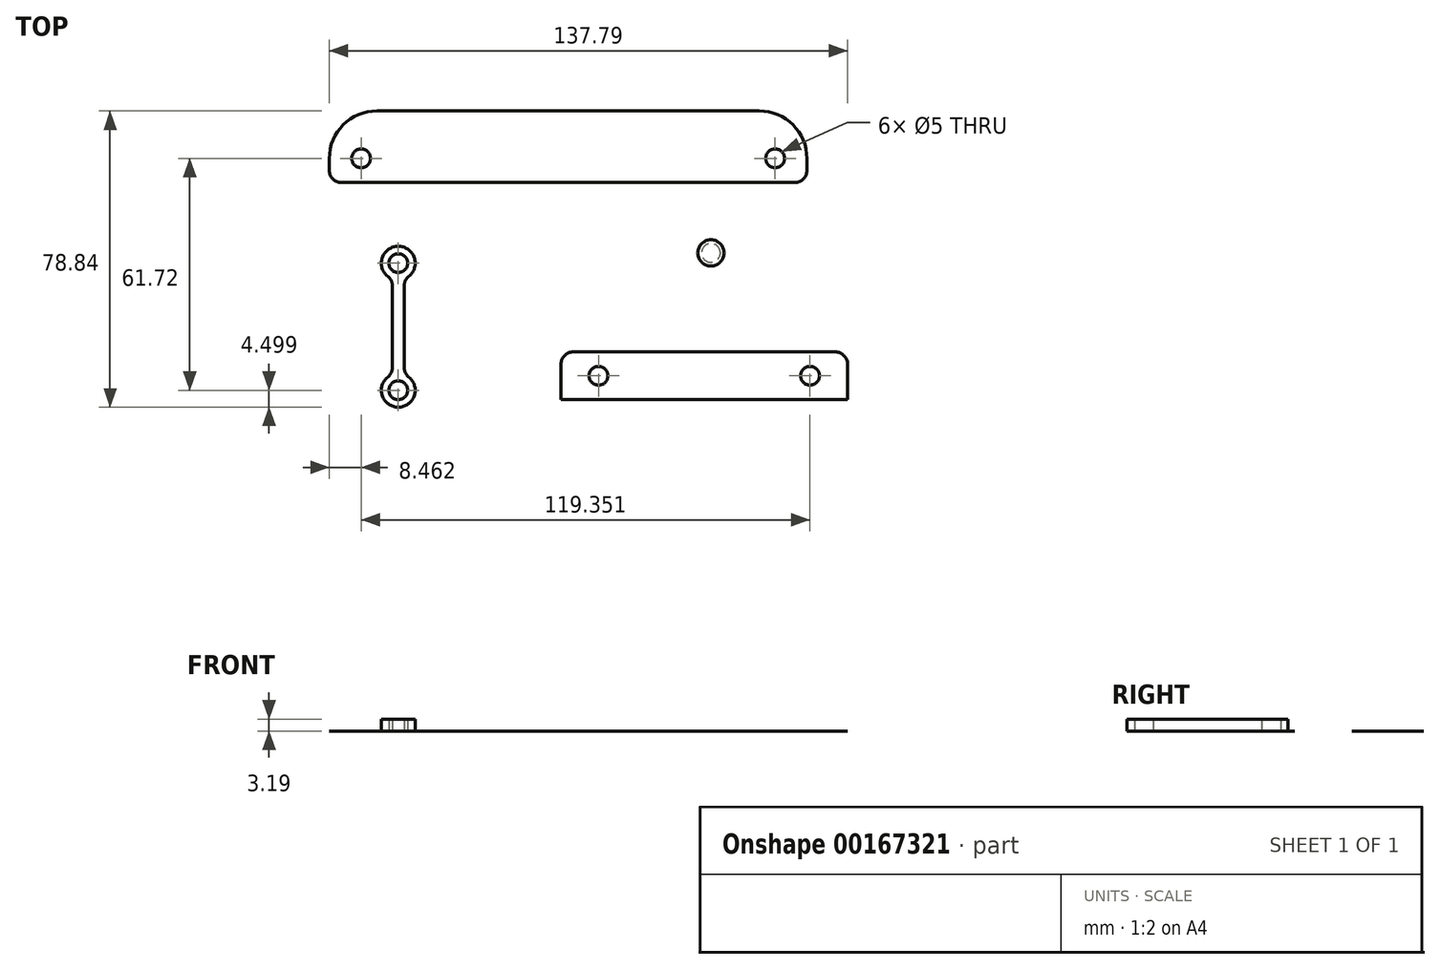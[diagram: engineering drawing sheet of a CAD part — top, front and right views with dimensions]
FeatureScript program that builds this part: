
annotation { "Feature Type Name" : "Feature", "Feature Type Description" : "" }
export const myFeature = defineFeature(function(context is Context, id is Id, definition is map)
    precondition{}
    {
        {
            var Q0;
            Q0=qCreatedBy(makeId("Top.planeOp"),FACE);
            var sketch = newSketch(context, id + "F0", { "sketchPlane" : qUnion([Q0])});
            skCircle(sketch, "E0", {"center": v(-35.3, 16.91) * mm, "radius": 2.5 * mm});
            skArc(sketch, "E1", {"start": v(-32.5, 13.38) * mm, "mid": v(-35.3, 21.41) * mm, "end": v(-38.09, 13.38) * mm});
            skLineSegment(sketch, "E2.bottom", {"start": v(-33.71, 0) * mm, "end": v(-36.88, 0) * mm});
            skLineSegment(sketch, "E2.left", {"start": v(-33.71, 0) * mm, "end": v(-33.71, 10.9) * mm});
            skLineSegment(sketch, "E2.right", {"start": v(-36.88, 0) * mm, "end": v(-36.88, 10.9) * mm});
            skPoint(sketch, "E3.visualSharp", {"position": v(-36.88, 12.7) * mm});
            skArc(sketch, "E3.filletArc", {"start": v(-36.88, 10.9) * mm, "mid": v(-37.2, 12.27) * mm, "end": v(-38.09, 13.38) * mm});
            skPoint(sketch, "E4.visualSharp", {"position": v(-33.71, 12.7) * mm});
            skArc(sketch, "E4.filletArc", {"start": v(-32.5, 13.38) * mm, "mid": v(-33.4, 12.27) * mm, "end": v(-33.71, 10.9) * mm});
            skArc(sketch, "E5.MirrorCS", {"start": v(-36.88, -10.9) * mm, "mid": v(-37.2, -12.27) * mm, "end": v(-38.09, -13.38) * mm});
            skPoint(sketch, "E6.MirrorP", {"position": v(-36.88, -12.7) * mm});
            skCircle(sketch, "E7.MirrorC", {"center": v(-35.3, -16.91) * mm, "radius": 2.5 * mm});
            skLineSegment(sketch, "E8.MirrorCS", {"start": v(-33.71, 0) * mm, "end": v(-33.71, -10.9) * mm});
            skLineSegment(sketch, "E9.MirrorCS", {"start": v(-36.88, 0) * mm, "end": v(-36.88, -10.9) * mm});
            skArc(sketch, "E10.MirrorCS", {"start": v(-32.5, -13.38) * mm, "mid": v(-33.4, -12.27) * mm, "end": v(-33.71, -10.9) * mm});
            skArc(sketch, "E11.MirrorCS", {"start": v(-32.5, -13.38) * mm, "mid": v(-35.3, -21.41) * mm, "end": v(-38.09, -13.38) * mm});
            skPoint(sketch, "E12.MirrorP", {"position": v(-33.71, -12.7) * mm});
            skSolve(sketch);
        }
        {
            var Q0;
            Q0 = qSketchRegion(id + "F0", true);
            extrude(context, id + "F1", {"entities" : qUnion([Q0]), "depth" : 3.17 * mm});
        }
        {
            var Q0;
            Q0=qCreatedBy(makeId("Top.planeOp"),FACE);
            var sketch = newSketch(context, id + "F2", { "sketchPlane" : qUnion([Q0])});
            skLineSegment(sketch, "E13.bottom", {"start": v(-50.47, 38.38) * mm, "end": v(9.86, 38.38) * mm});
            skLineSegment(sketch, "E13.top", {"start": v(-40.94, 57.43) * mm, "end": v(9.86, 57.43) * mm});
            skLineSegment(sketch, "E13.left", {"start": v(-53.64, 41.56) * mm, "end": v(-53.64, 44.73) * mm});
            skLineSegment(sketch, "E13.right", {"start": v(9.86, 38.38) * mm, "end": v(9.86, 57.43) * mm, "construction": true});
            skCircle(sketch, "E14", {"center": v(-45.18, 44.8) * mm, "radius": 2.5 * mm});
            skPoint(sketch, "E15.visualSharp", {"position": v(-53.64, 57.43) * mm});
            skArc(sketch, "E15.filletArc", {"start": v(-40.94, 57.43) * mm, "mid": v(-49.92, 53.71) * mm, "end": v(-53.64, 44.73) * mm});
            skPoint(sketch, "E16.visualSharp", {"position": v(-53.64, 38.38) * mm});
            skArc(sketch, "E16.filletArc", {"start": v(-53.64, 41.56) * mm, "mid": v(-52.71, 39.31) * mm, "end": v(-50.47, 38.38) * mm});
            skLineSegment(sketch, "E17.MirrorCS", {"start": v(70.18, 38.38) * mm, "end": v(9.86, 38.38) * mm});
            skLineSegment(sketch, "E18.MirrorCS", {"start": v(60.66, 57.43) * mm, "end": v(9.86, 57.43) * mm});
            skLineSegment(sketch, "E19.MirrorCS", {"start": v(73.36, 41.56) * mm, "end": v(73.36, 44.73) * mm});
            skArc(sketch, "E20.MirrorCS", {"start": v(73.36, 41.56) * mm, "mid": v(72.43, 39.31) * mm, "end": v(70.18, 38.38) * mm});
            skCircle(sketch, "E21.MirrorC", {"center": v(64.9, 44.8) * mm, "radius": 2.5 * mm});
            skPoint(sketch, "E22.MirrorP", {"position": v(73.36, 38.38) * mm});
            skArc(sketch, "E23.MirrorCS", {"start": v(60.66, 57.43) * mm, "mid": v(69.64, 53.71) * mm, "end": v(73.36, 44.73) * mm});
            skPoint(sketch, "E24.MirrorP", {"position": v(73.36, 57.43) * mm});
            skSolve(sketch);
        }
        {
            var Q0;
            Q0 = qSketchRegion(id + "F2", true);
            extrude(context, id + "F3", {"entities" : qUnion([Q0]), "depth" : 1 / 203.2 * mm});
        }
        {
            var Q0;
            Q0=qCreatedBy(makeId("Top.planeOp"),FACE);
            var sketch = newSketch(context, id + "F4", { "sketchPlane" : qUnion([Q0])});
            skCircle(sketch, "E25", {"center": v(47.83, 19.63) * mm, "radius": 2.5 * mm});
            skCircle(sketch, "E26", {"center": v(47.83, 19.63) * mm, "radius": 3.5 * mm});
            skSolve(sketch);
        }
        {
            var Q0;
            Q0=makeQuery(id+"F4.imprint","IMPRINT",FACE,{"disambiguationData":[TD([[makeQuery(id+"F4.imprint","IMPRINT",EDGE,{"derivedFrom":sQuery(id+"F4.wireOp",EDGE,"E25")}),1.0]])]});
            extrude(context, id + "F5", {"entities" : qUnion([Q0]), "oppositeDirection" : true, "depth" : 1 / 101.6 * mm});
        }
        {
            var Q0;
            Q0=makeQuery(id+"F4.imprint","IMPRINT",FACE,{"disambiguationData":[TD([[makeQuery(id+"F4.imprint","IMPRINT",EDGE,{"derivedFrom":sQuery(id+"F4.wireOp",EDGE,"E25")}),1.0]])]});
            var Q1;
            Q1=makeQuery(id+"F4.imprint","IMPRINT",FACE,{"disambiguationData":[TD([[makeQuery(id+"F4.imprint","IMPRINT",EDGE,{"derivedFrom":sQuery(id+"F4.wireOp",EDGE,"E25")}),-1.0]])]});
            extrude(context, id + "F6", {"entities" : qUnion([Q0, Q1]), "operationType" : NewBodyOperationType.ADD, "depth" : 1 / 203.2 * mm});
        }
        {
            var Q0;
            Q0=qCreatedBy(makeId("Top.planeOp"),FACE);
            var sketch = newSketch(context, id + "F7", { "sketchPlane" : qUnion([Q0])});
            skLineSegment(sketch, "E27.bottom", {"start": v(11.24, -6.7) * mm, "end": v(46.05, -6.7) * mm});
            skLineSegment(sketch, "E27.top", {"start": v(7.95, -19.4) * mm, "end": v(46.05, -19.4) * mm});
            skLineSegment(sketch, "E27.left", {"start": v(7.95, -10) * mm, "end": v(7.95, -19.4) * mm});
            skLineSegment(sketch, "E27.right", {"start": v(46.05, -6.7) * mm, "end": v(46.05, -19.4) * mm, "construction": true});
            skPoint(sketch, "E28.visualSharp", {"position": v(7.95, -6.7) * mm});
            skArc(sketch, "E28.filletArc", {"start": v(11.24, -6.7) * mm, "mid": v(8.92, -7.67) * mm, "end": v(7.95, -10) * mm});
            skCircle(sketch, "E29", {"center": v(17.94, -13.06) * mm, "radius": 2.5 * mm});
            skLineSegment(sketch, "E30", {"start": v(17.94, -13.06) * mm, "end": v(17.94, -19.4) * mm});
            skLineSegment(sketch, "E31", {"start": v(17.94, -19.4) * mm, "end": v(17.94, -13.06) * mm, "construction": true});
            skLineSegment(sketch, "E32", {"start": v(17.94, -13.06) * mm, "end": v(17.94, -6.7) * mm, "construction": true});
            skLineSegment(sketch, "E33.MirrorCS", {"start": v(74.17, -13.06) * mm, "end": v(74.17, -19.4) * mm});
            skLineSegment(sketch, "E34.MirrorCS", {"start": v(80.86, -6.7) * mm, "end": v(46.05, -6.7) * mm});
            skLineSegment(sketch, "E35.MirrorCS", {"start": v(84.15, -19.4) * mm, "end": v(46.05, -19.4) * mm});
            skLineSegment(sketch, "E36.MirrorCS", {"start": v(84.15, -10) * mm, "end": v(84.15, -19.4) * mm});
            skLineSegment(sketch, "E37.MirrorCS", {"start": v(74.17, -13.06) * mm, "end": v(74.17, -6.7) * mm, "construction": true});
            skLineSegment(sketch, "E38.MirrorCS", {"start": v(74.17, -19.4) * mm, "end": v(74.17, -13.06) * mm, "construction": true});
            skPoint(sketch, "E39.MirrorP", {"position": v(84.15, -6.7) * mm});
            skCircle(sketch, "E40.MirrorC", {"center": v(74.17, -13.06) * mm, "radius": 2.5 * mm});
            skArc(sketch, "E41.MirrorCS", {"start": v(80.86, -6.7) * mm, "mid": v(83.2, -7.67) * mm, "end": v(84.15, -10) * mm});
            skSolve(sketch);
        }
        {
            var Q0;
            Q0 = qSketchRegion(id + "F7", true);
            extrude(context, id + "F8", {"entities" : qUnion([Q0]), "depth" : 1 / 203.2 * mm});
        }
    });
